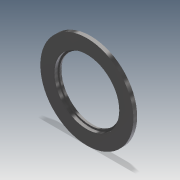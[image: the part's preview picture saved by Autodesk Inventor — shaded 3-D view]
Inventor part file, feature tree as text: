
AUTODESK INVENTOR PART (.ipt)
format: ipt  version: 2021 (Build 250183000, 183)  size: 143,360 bytes
history: native  units: mm (DEFAULTED — no unit token found)
features: sketch x4, extrude x3, hole x1
ambient origin geometry x8: Origin, YZ Plane, XZ Plane, XY Plane, X Axis, Y Axis, Z Axis, Center Point
bodies: Solid1 (feature_tree)
feature tree (8):
  extrude  "Extrusion1"  Depth=3.048mm TaperAngle=0.0deg
  extrude  "Extrusion2"  Depth=52.197mm
  extrude  "Extrusion3"  [1 undecoded]
  hole  "Hole1"  [1 undecoded]
  sketch  "Sketch2"  dims[d0=75.0062mm d1=3.048mm d2=0.0mm]
  sketch  "Sketch3"  dims[d3=2.032mm d4=-13.089969mm d5=52.197mm]
  sketch  "Sketch4"  dims[d6=2.54mm d7=0.0mm]
  sketch  "Sketch5"  dims[d8=49.2252mm d9=12.7mm d10=51.054mm d11=1.27mm d12=14.3117mm d13=19.05mm d14=20.594885mm]
note: 2 required parameter values undecoded (feature->parameter linkage not recoverable at this tier; creation-order binding heuristic only, values carry confidence <= 0.55)
